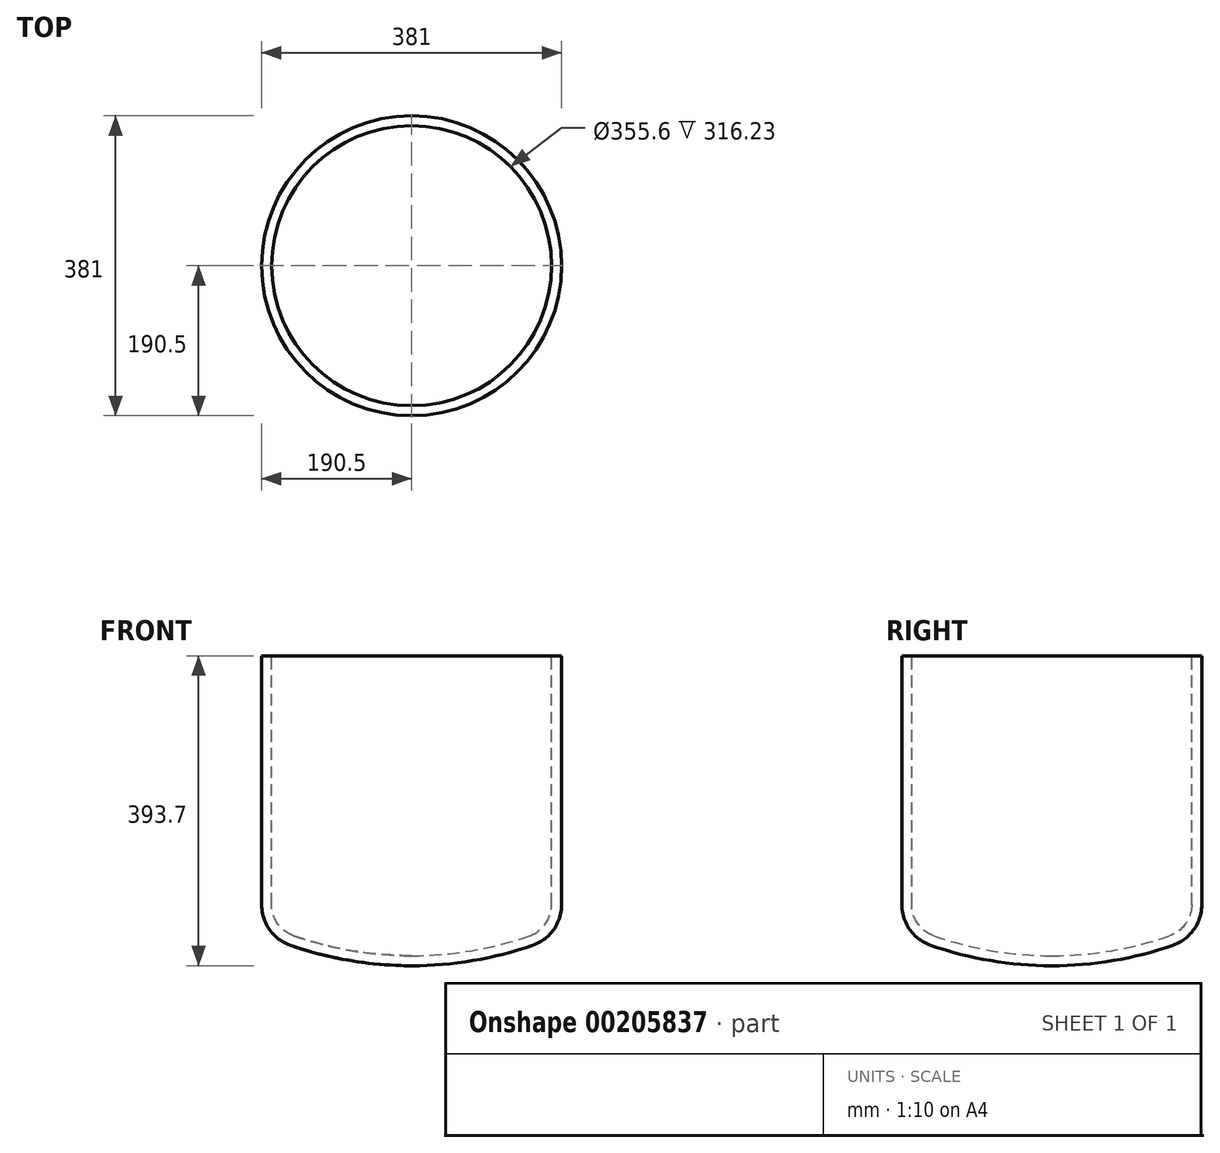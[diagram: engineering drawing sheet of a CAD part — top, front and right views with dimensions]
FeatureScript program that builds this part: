
annotation { "Feature Type Name" : "Feature", "Feature Type Description" : "" }
export const myFeature = defineFeature(function(context is Context, id is Id, definition is map)
    precondition{}
    {
        {
            var Q0;
            Q0=qCreatedBy(makeId("Front.planeOp"),FACE);
            var sketch = newSketch(context, id + "F0", { "sketchPlane" : qUnion([Q0])});
            skLineSegment(sketch, "E0", {"start": v(-190.5, 158.12) * mm, "end": v(-190.5, -158.12) * mm});
            skLineSegment(sketch, "E1", {"start": v(-190.5, 158.12) * mm, "end": v(-177.8, 158.12) * mm});
            skLineSegment(sketch, "E2", {"start": v(-177.8, 158.12) * mm, "end": v(-177.8, -158.12) * mm});
            skLineSegment(sketch, "E3", {"start": v(0, 158.12) * mm, "end": v(0, -158.12) * mm});
            skArc(sketch, "E4", {"start": v(-177.8, -158.12) * mm, "mid": v(-170.07, -182.34) * mm, "end": v(-149.73, -197.6) * mm});
            skArc(sketch, "E5", {"start": v(-190.5, -158.12) * mm, "mid": v(-180.42, -189.7) * mm, "end": v(-153.9, -209.6) * mm});
            skArc(sketch, "E6", {"start": v(-149.73, -197.6) * mm, "mid": v(-75.92, -216.52) * mm, "end": v(0, -222.88) * mm});
            skArc(sketch, "E7", {"start": v(-153.9, -209.6) * mm, "mid": v(-78.04, -229.04) * mm, "end": v(0, -235.58) * mm});
            skLineSegment(sketch, "E8", {"start": v(0, -235.58) * mm, "end": v(0, -222.88) * mm});
            skSolve(sketch);
        }
        {
            var Q0;
            Q0 = qSketchRegion(id + "F0", true);
            var Q1;
            Q1=sQuery(id+"F0.wireOp",EDGE,"E3");
            revolve(context, id + "F1", {"entities" : qUnion([Q0]), "axis" : qUnion([Q1]), "revolveType" : RevolveType.FULL});
        }
    });
